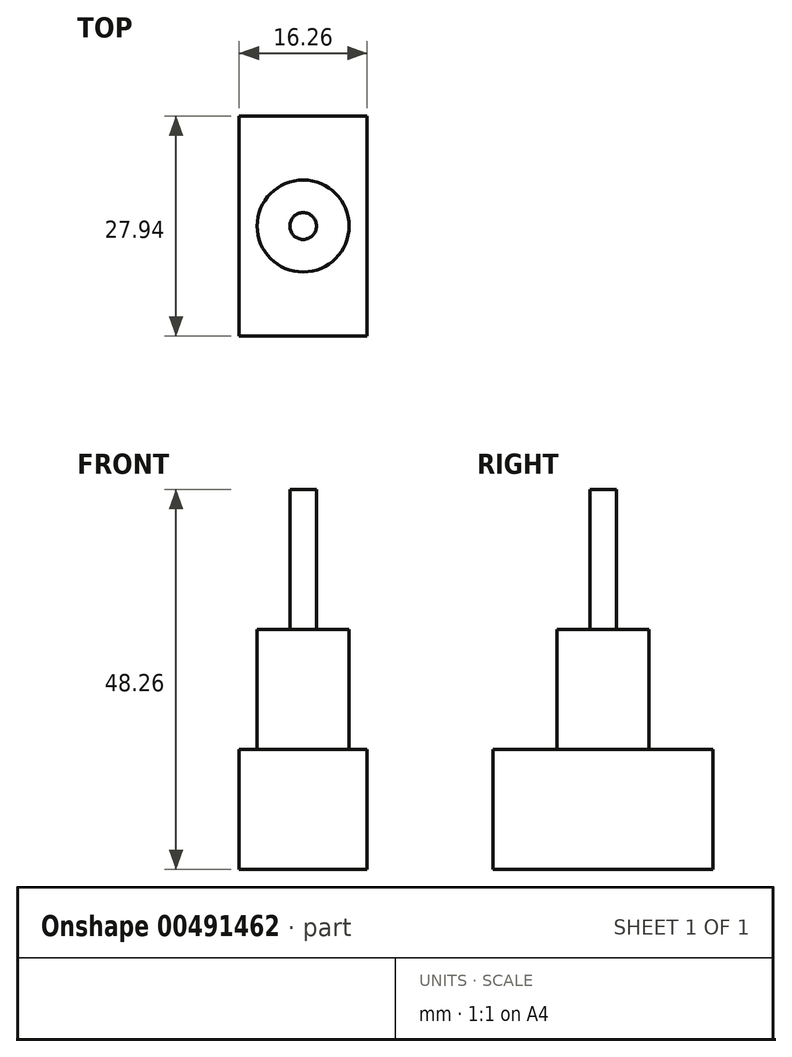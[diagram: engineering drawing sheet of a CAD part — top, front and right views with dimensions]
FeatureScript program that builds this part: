
annotation { "Feature Type Name" : "Feature", "Feature Type Description" : "" }
export const myFeature = defineFeature(function(context is Context, id is Id, definition is map)
    precondition{}
    {
        {
            var Q0;
            Q0=qCreatedBy(makeId("Top.planeOp"),FACE);
            var sketch = newSketch(context, id + "F0", { "sketchPlane" : qUnion([Q0])});
            skCircle(sketch, "E0", {"center": v(0, 0) * mm, "radius": 5.84 * mm});
            skSolve(sketch);
        }
        {
            var Q0;
            Q0=makeQuery(id+"F0.imprint","IMPRINT",FACE,{"disambiguationData":[TD([[makeQuery(id+"F0.imprint","IMPRINT",EDGE,{"derivedFrom":sQuery(id+"F0.wireOp",EDGE,"E0")}),1.0]])]});
            extrude(context, id + "F1", {"entities" : qUnion([Q0]), "depth" : 15.24 * mm});
        }
        {
            var Q0;
            Q0=makeQuery(id+"F1.opExtrude","CAP_FACE",FACE,{"disambiguationData":[OSD([sQuery(id+"F0.wireOp",EDGE,"E0")])],"isStart":false});
            var sketch = newSketch(context, id + "F2", { "sketchPlane" : qUnion([Q0])});
            skCircle(sketch, "E1", {"center": v(0, 0) * mm, "radius": 1.7 * mm});
            skSolve(sketch);
        }
        {
            var Q0;
            Q0=makeQuery(id+"F2.imprint","IMPRINT",FACE,{"disambiguationData":[TD([[makeQuery(id+"F2.imprint","IMPRINT",EDGE,{"derivedFrom":sQuery(id+"F2.wireOp",EDGE,"E1")}),1.0]])]});
            extrude(context, id + "F3", {"entities" : qUnion([Q0]), "operationType" : NewBodyOperationType.ADD, "depth" : 17.78 * mm});
        }
        {
            var Q0;
            Q0=qCreatedBy(makeId("Top.planeOp"),FACE);
            var sketch = newSketch(context, id + "F4", { "sketchPlane" : qUnion([Q0])});
            skLineSegment(sketch, "E2.bottom", {"start": v(-8.13, -13.97) * mm, "end": v(8.13, -13.97) * mm});
            skLineSegment(sketch, "E2.top", {"start": v(-8.13, 13.97) * mm, "end": v(8.13, 13.97) * mm});
            skLineSegment(sketch, "E2.left", {"start": v(-8.13, -13.97) * mm, "end": v(-8.13, 13.97) * mm});
            skLineSegment(sketch, "E2.right", {"start": v(8.13, -13.97) * mm, "end": v(8.13, 13.97) * mm});
            skPoint(sketch, "E2.middle", {"position": v(0, 0) * mm});
            skSolve(sketch);
        }
        {
            var Q0;
            Q0=makeQuery(id+"F4.imprint","IMPRINT",FACE,{"disambiguationData":[TD([[makeQuery(id+"F4.imprint","IMPRINT",EDGE,{"derivedFrom":sQuery(id+"F4.wireOp",EDGE,"E2.bottom")}),1.0]])]});
            extrude(context, id + "F5", {"entities" : qUnion([Q0]), "operationType" : NewBodyOperationType.ADD, "oppositeDirection" : true, "depth" : 15.24 * mm});
        }
    });
